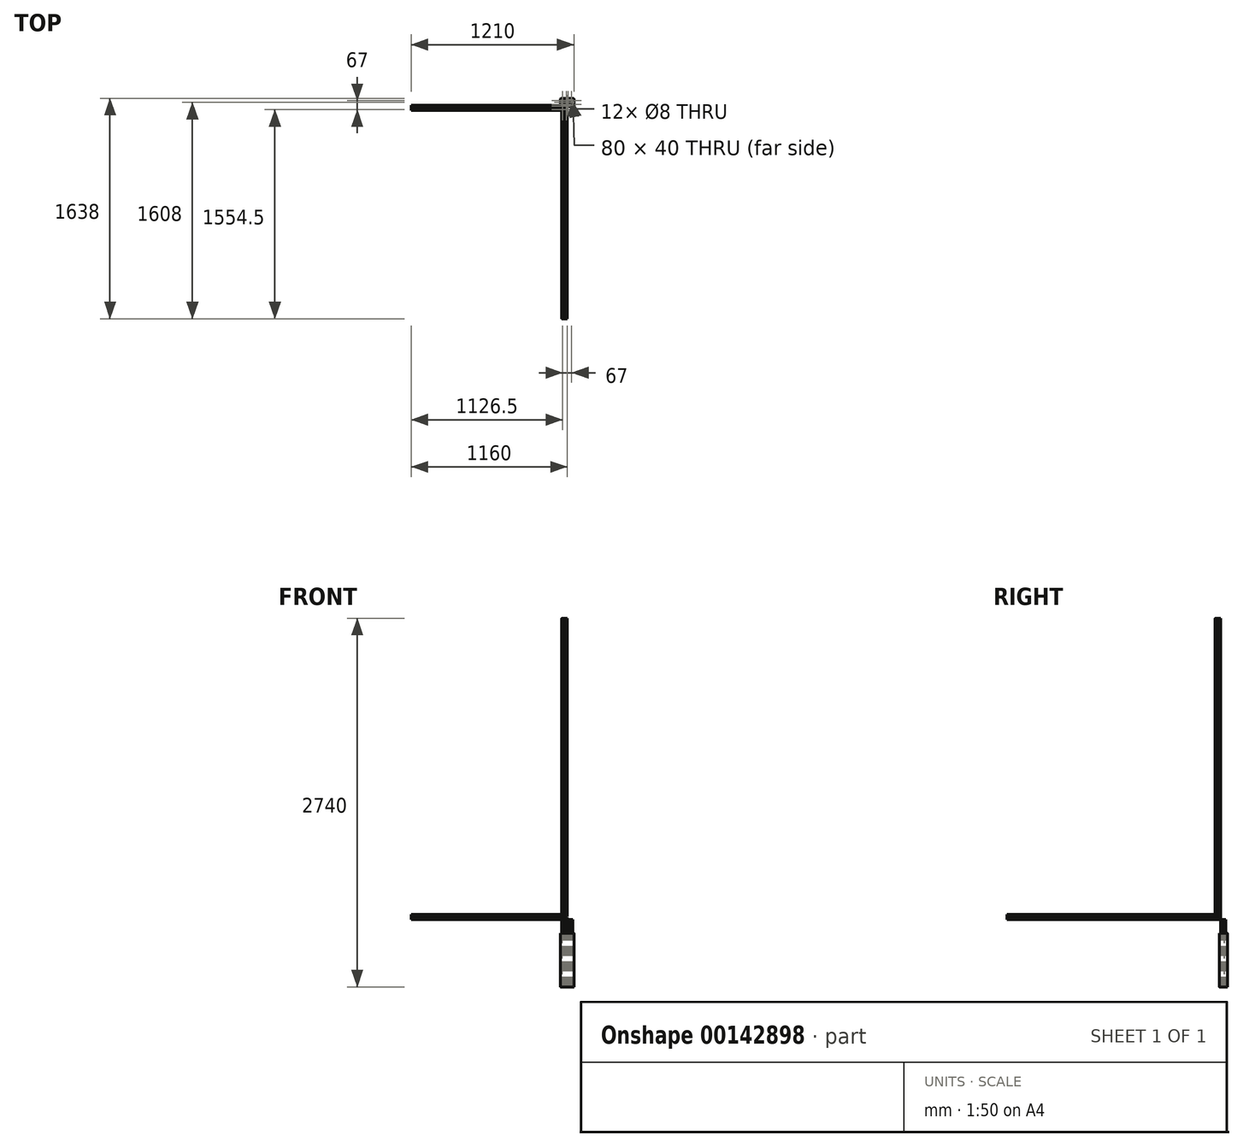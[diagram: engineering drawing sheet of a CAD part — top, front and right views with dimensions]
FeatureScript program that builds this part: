
annotation { "Feature Type Name" : "Feature", "Feature Type Description" : "" }
export const myFeature = defineFeature(function(context is Context, id is Id, definition is map)
    precondition{}
    {
        {
            var Q0;
            Q0=qCreatedBy(makeId("Front.planeOp"),FACE);
            var sketch = newSketch(context, id + "F0", { "sketchPlane" : qUnion([Q0])});
            skArc(sketch, "E0", {"start": v(-0.25, 3.4) * mm, "mid": v(-2.94, 1.7) * mm, "end": v(-3.06, -1.48) * mm});
            skArc(sketch, "E1", {"start": v(0.25, 3.4) * mm, "mid": v(0, 3.65) * mm, "end": v(-0.25, 3.4) * mm});
            skArc(sketch, "E2.1.0", {"start": v(-3.06, -1.48) * mm, "mid": v(-3.16, -1.82) * mm, "end": v(-2.81, -1.91) * mm});
            skArc(sketch, "E2.2.0", {"start": v(2.81, -1.91) * mm, "mid": v(3.16, -1.82) * mm, "end": v(3.06, -1.48) * mm});
            skArc(sketch, "E3.trimOffspring", {"start": v(3.06, -1.48) * mm, "mid": v(2.94, 1.7) * mm, "end": v(0.25, 3.4) * mm});
            skArc(sketch, "E4.trimOffspring", {"start": v(-2.81, -1.91) * mm, "mid": v(0, -3.4) * mm, "end": v(2.81, -1.91) * mm});
            skCircle(sketch, "E5", {"center": v(-13.5, 13.5) * mm, "radius": 4 * mm});
            skCircle(sketch, "E6.1.0", {"center": v(-13.5, -13.5) * mm, "radius": 4 * mm});
            skCircle(sketch, "E6.2.0", {"center": v(13.5, -13.5) * mm, "radius": 4 * mm});
            skCircle(sketch, "E6.3.0", {"center": v(13.5, 13.5) * mm, "radius": 4 * mm});
            skLineSegment(sketch, "E7.rect.bottom", {"start": v(19, -20) * mm, "end": v(-19, -20) * mm});
            skLineSegment(sketch, "E7.rect.top", {"start": v(19, 20) * mm, "end": v(4.2, 20) * mm});
            skLineSegment(sketch, "E7.rect.left", {"start": v(20, -19) * mm, "end": v(20, 19) * mm});
            skLineSegment(sketch, "E7.rect.right", {"start": v(-20, -19) * mm, "end": v(-20, 19) * mm});
            skPoint(sketch, "E8.visualSharp", {"position": v(-20, 20) * mm});
            skArc(sketch, "E8.filletArc", {"start": v(-19, 20) * mm, "mid": v(-19.7, 19.7) * mm, "end": v(-20, 19) * mm});
            skPoint(sketch, "E9.visualSharp", {"position": v(20, 20) * mm});
            skArc(sketch, "E9.filletArc", {"start": v(20, 19) * mm, "mid": v(19.7, 19.7) * mm, "end": v(19, 20) * mm});
            skPoint(sketch, "E10.visualSharp", {"position": v(-20, -20) * mm});
            skArc(sketch, "E10.filletArc", {"start": v(-20, -19) * mm, "mid": v(-19.7, -19.7) * mm, "end": v(-19, -20) * mm});
            skPoint(sketch, "E11.visualSharp", {"position": v(20, -20) * mm});
            skArc(sketch, "E11.filletArc", {"start": v(19, -20) * mm, "mid": v(19.7, -19.7) * mm, "end": v(20, -19) * mm});
            skLineSegment(sketch, "E12.rect.bottom", {"start": v(-16, -4.2) * mm, "end": v(-20, -4.2) * mm});
            skLineSegment(sketch, "E12.rect.top", {"start": v(-16, 4.2) * mm, "end": v(-20, 4.2) * mm});
            skLineSegment(sketch, "E12.rect.right", {"start": v(-20, -4.2) * mm, "end": v(-20, 4.2) * mm});
            skPoint(sketch, "E12.rect.middle", {"position": v(-18, 0) * mm});
            skLineSegment(sketch, "E13.rect.bottom", {"start": v(-16, 7.25) * mm, "end": v(-9.36, 7.25) * mm});
            skLineSegment(sketch, "E13.rect.top", {"start": v(-16, -7.25) * mm, "end": v(-9.36, -7.25) * mm});
            skLineSegment(sketch, "E13.rect.left", {"start": v(-16, 7.25) * mm, "end": v(-16, 4.2) * mm});
            skPoint(sketch, "E13.rect.middle", {"position": v(-12.68, 0) * mm});
            skPoint(sketch, "E13.rect.middle.positionSnap0", {"position": v(-16, 0) * mm});
            skPoint(sketch, "E13.rect.cornerSnap0", {"position": v(-16, 0) * mm});
            skPoint(sketch, "E13.rect.centerSnap0", {"position": v(-16, 0) * mm});
            skLineSegment(sketch, "E14.trimOffspring", {"start": v(-16, -4.2) * mm, "end": v(-16, -7.25) * mm});
            skArc(sketch, "E15", {"start": v(-9.36, 7.25) * mm, "mid": v(-6, 0) * mm, "end": v(-9.36, -7.25) * mm});
            skLineSegment(sketch, "E16.1.0", {"start": v(4.2, -16) * mm, "end": v(7.25, -16) * mm});
            skLineSegment(sketch, "E16.1.1", {"start": v(4.2, -16) * mm, "end": v(4.2, -20) * mm});
            skPoint(sketch, "E16.1.2", {"position": v(0, -16) * mm});
            skLineSegment(sketch, "E16.1.3", {"start": v(-7.25, -16) * mm, "end": v(-4.2, -16) * mm});
            skPoint(sketch, "E16.1.4", {"position": v(0, -18) * mm});
            skLineSegment(sketch, "E16.1.5", {"start": v(7.25, -16) * mm, "end": v(7.25, -9.36) * mm});
            skArc(sketch, "E16.1.6", {"start": v(-7.25, -9.36) * mm, "mid": v(0, -6) * mm, "end": v(7.25, -9.36) * mm});
            skLineSegment(sketch, "E16.1.7", {"start": v(-7.25, -16) * mm, "end": v(-7.25, -9.36) * mm});
            skLineSegment(sketch, "E16.1.8", {"start": v(4.2, -20) * mm, "end": v(-4.2, -20) * mm});
            skLineSegment(sketch, "E16.1.9", {"start": v(-4.2, -16) * mm, "end": v(-4.2, -20) * mm});
            skPoint(sketch, "E16.1.10", {"position": v(0, -12.68) * mm});
            skPoint(sketch, "E16.1.11", {"position": v(0, -16) * mm});
            skPoint(sketch, "E16.1.12", {"position": v(0, -16) * mm});
            skLineSegment(sketch, "E16.2.0", {"start": v(16, 4.2) * mm, "end": v(16, 7.25) * mm});
            skLineSegment(sketch, "E16.2.1", {"start": v(16, 4.2) * mm, "end": v(20, 4.2) * mm});
            skPoint(sketch, "E16.2.2", {"position": v(16, 0) * mm});
            skLineSegment(sketch, "E16.2.3", {"start": v(16, -7.25) * mm, "end": v(16, -4.2) * mm});
            skPoint(sketch, "E16.2.4", {"position": v(18, 0) * mm});
            skLineSegment(sketch, "E16.2.5", {"start": v(16, 7.25) * mm, "end": v(9.36, 7.25) * mm});
            skArc(sketch, "E16.2.6", {"start": v(9.36, -7.25) * mm, "mid": v(6, 0) * mm, "end": v(9.36, 7.25) * mm});
            skLineSegment(sketch, "E16.2.7", {"start": v(16, -7.25) * mm, "end": v(9.36, -7.25) * mm});
            skLineSegment(sketch, "E16.2.8", {"start": v(20, 4.2) * mm, "end": v(20, -4.2) * mm});
            skLineSegment(sketch, "E16.2.9", {"start": v(16, -4.2) * mm, "end": v(20, -4.2) * mm});
            skPoint(sketch, "E16.2.10", {"position": v(12.68, 0) * mm});
            skPoint(sketch, "E16.2.11", {"position": v(16, 0) * mm});
            skPoint(sketch, "E16.2.12", {"position": v(16, 0) * mm});
            skLineSegment(sketch, "E16.3.0", {"start": v(-4.2, 16) * mm, "end": v(-7.25, 16) * mm});
            skLineSegment(sketch, "E16.3.1", {"start": v(-4.2, 16) * mm, "end": v(-4.2, 20) * mm});
            skPoint(sketch, "E16.3.2", {"position": v(0, 16) * mm});
            skLineSegment(sketch, "E16.3.3", {"start": v(7.25, 16) * mm, "end": v(4.2, 16) * mm});
            skPoint(sketch, "E16.3.4", {"position": v(0, 18) * mm});
            skLineSegment(sketch, "E16.3.5", {"start": v(-7.25, 16) * mm, "end": v(-7.25, 9.36) * mm});
            skArc(sketch, "E16.3.6", {"start": v(7.25, 9.36) * mm, "mid": v(0, 6) * mm, "end": v(-7.25, 9.36) * mm});
            skLineSegment(sketch, "E16.3.7", {"start": v(7.25, 16) * mm, "end": v(7.25, 9.36) * mm});
            skLineSegment(sketch, "E16.3.8", {"start": v(-4.2, 20) * mm, "end": v(4.2, 20) * mm});
            skLineSegment(sketch, "E16.3.9", {"start": v(4.2, 16) * mm, "end": v(4.2, 20) * mm});
            skPoint(sketch, "E16.3.10", {"position": v(0, 12.68) * mm});
            skPoint(sketch, "E16.3.11", {"position": v(0, 16) * mm});
            skPoint(sketch, "E16.3.12", {"position": v(0, 16) * mm});
            skLineSegment(sketch, "E17.trimOffspring", {"start": v(-4.2, 20) * mm, "end": v(-19, 20) * mm});
            skSolve(sketch);
        }
        {
            var Q0;
            Q0=makeQuery(id+"F0.imprint","IMPRINT",FACE,{"disambiguationData":[TD([[makeQuery(id+"F0.imprint","IMPRINT",EDGE,{"derivedFrom":sQuery(id+"F0.wireOp",EDGE,"E0")}),-1.0]])]});
            extrude(context, id + "F1", {"entities" : qUnion([Q0]), "depth" : 1588 * mm});
        }
        {
            var Q0;
            Q0=makeQuery(id+"F0.imprint","IMPRINT",FACE,{"disambiguationData":[TD([[makeQuery(id+"F0.imprint","IMPRINT",EDGE,{"derivedFrom":sQuery(id+"F0.wireOp",EDGE,"E0")}),-1.0]])]});
            extrude(context, id + "F2", {"entities" : qUnion([Q0]), "depth" : 2200 * mm});
        }
        {
            var Q0;
            Q0=makeQuery(id+"F2.opExtrude","SWEPT_BODY",BODY,{"disambiguationData":[OSD([sQuery(id+"F0.wireOp",EDGE,"E0"),sQuery(id+"F0.wireOp",EDGE,"E1"),sQuery(id+"F0.wireOp",EDGE,"E2.1.0"),sQuery(id+"F0.wireOp",EDGE,"E2.2.0"),sQuery(id+"F0.wireOp",EDGE,"E3.trimOffspring"),sQuery(id+"F0.wireOp",EDGE,"E4.trimOffspring"),sQuery(id+"F0.wireOp",EDGE,"E5"),sQuery(id+"F0.wireOp",EDGE,"E6.1.0"),sQuery(id+"F0.wireOp",EDGE,"E6.2.0"),sQuery(id+"F0.wireOp",EDGE,"E6.3.0"),sQuery(id+"F0.wireOp",EDGE,"E7.rect.bottom"),sQuery(id+"F0.wireOp",EDGE,"E7.rect.top"),sQuery(id+"F0.wireOp",EDGE,"E7.rect.left"),sQuery(id+"F0.wireOp",EDGE,"E7.rect.right"),sQuery(id+"F0.wireOp",EDGE,"E8.filletArc"),sQuery(id+"F0.wireOp",EDGE,"E9.filletArc"),sQuery(id+"F0.wireOp",EDGE,"E10.filletArc"),sQuery(id+"F0.wireOp",EDGE,"E11.filletArc"),sQuery(id+"F0.wireOp",EDGE,"E12.rect.bottom"),sQuery(id+"F0.wireOp",EDGE,"E12.rect.top"),sQuery(id+"F0.wireOp",EDGE,"E13.rect.bottom"),sQuery(id+"F0.wireOp",EDGE,"E13.rect.top"),sQuery(id+"F0.wireOp",EDGE,"E13.rect.left"),sQuery(id+"F0.wireOp",EDGE,"E14.trimOffspring"),sQuery(id+"F0.wireOp",EDGE,"E15"),sQuery(id+"F0.wireOp",EDGE,"E16.1.0"),sQuery(id+"F0.wireOp",EDGE,"E16.1.1"),sQuery(id+"F0.wireOp",EDGE,"E16.1.3"),sQuery(id+"F0.wireOp",EDGE,"E16.1.5"),sQuery(id+"F0.wireOp",EDGE,"E16.1.6"),sQuery(id+"F0.wireOp",EDGE,"E16.1.7"),sQuery(id+"F0.wireOp",EDGE,"E16.1.9"),sQuery(id+"F0.wireOp",EDGE,"E16.2.0"),sQuery(id+"F0.wireOp",EDGE,"E16.2.1"),sQuery(id+"F0.wireOp",EDGE,"E16.2.3"),sQuery(id+"F0.wireOp",EDGE,"E16.2.5"),sQuery(id+"F0.wireOp",EDGE,"E16.2.6"),sQuery(id+"F0.wireOp",EDGE,"E16.2.7"),sQuery(id+"F0.wireOp",EDGE,"E16.2.9"),sQuery(id+"F0.wireOp",EDGE,"E16.3.0"),sQuery(id+"F0.wireOp",EDGE,"E16.3.1"),sQuery(id+"F0.wireOp",EDGE,"E16.3.3"),sQuery(id+"F0.wireOp",EDGE,"E16.3.5"),sQuery(id+"F0.wireOp",EDGE,"E16.3.6"),sQuery(id+"F0.wireOp",EDGE,"E16.3.7"),sQuery(id+"F0.wireOp",EDGE,"E16.3.9"),sQuery(id+"F0.wireOp",EDGE,"E17.trimOffspring")])]});
            var Q1;
            Q1=sQuery(id+"F0.wireOp",EDGE,"E7.rect.top");
            transform(context, id + "F3", {"entities" : qUnion([Q0]), "transformType" : TransformType.ROTATION, "transformAxis" : qUnion([Q1]), "angle" : 90 * degree, "makeCopy" : false});
        }
        {
            var Q0;
            Q0=makeQuery(id+"F0.imprint","IMPRINT",FACE,{"disambiguationData":[TD([[makeQuery(id+"F0.imprint","IMPRINT",EDGE,{"derivedFrom":sQuery(id+"F0.wireOp",EDGE,"E0")}),-1.0]])]});
            extrude(context, id + "F4", {"entities" : qUnion([Q0]), "depth" : 1120 * mm});
        }
        {
            var Q0;
            Q0=makeQuery(id+"F4.opExtrude","SWEPT_BODY",BODY,{"disambiguationData":[OSD([sQuery(id+"F0.wireOp",EDGE,"E0"),sQuery(id+"F0.wireOp",EDGE,"E1"),sQuery(id+"F0.wireOp",EDGE,"E2.1.0"),sQuery(id+"F0.wireOp",EDGE,"E2.2.0"),sQuery(id+"F0.wireOp",EDGE,"E3.trimOffspring"),sQuery(id+"F0.wireOp",EDGE,"E4.trimOffspring"),sQuery(id+"F0.wireOp",EDGE,"E5"),sQuery(id+"F0.wireOp",EDGE,"E6.1.0"),sQuery(id+"F0.wireOp",EDGE,"E6.2.0"),sQuery(id+"F0.wireOp",EDGE,"E6.3.0"),sQuery(id+"F0.wireOp",EDGE,"E7.rect.bottom"),sQuery(id+"F0.wireOp",EDGE,"E7.rect.top"),sQuery(id+"F0.wireOp",EDGE,"E7.rect.left"),sQuery(id+"F0.wireOp",EDGE,"E7.rect.right"),sQuery(id+"F0.wireOp",EDGE,"E8.filletArc"),sQuery(id+"F0.wireOp",EDGE,"E9.filletArc"),sQuery(id+"F0.wireOp",EDGE,"E10.filletArc"),sQuery(id+"F0.wireOp",EDGE,"E11.filletArc"),sQuery(id+"F0.wireOp",EDGE,"E12.rect.bottom"),sQuery(id+"F0.wireOp",EDGE,"E12.rect.top"),sQuery(id+"F0.wireOp",EDGE,"E13.rect.bottom"),sQuery(id+"F0.wireOp",EDGE,"E13.rect.top"),sQuery(id+"F0.wireOp",EDGE,"E13.rect.left"),sQuery(id+"F0.wireOp",EDGE,"E14.trimOffspring"),sQuery(id+"F0.wireOp",EDGE,"E15"),sQuery(id+"F0.wireOp",EDGE,"E16.1.0"),sQuery(id+"F0.wireOp",EDGE,"E16.1.1"),sQuery(id+"F0.wireOp",EDGE,"E16.1.3"),sQuery(id+"F0.wireOp",EDGE,"E16.1.5"),sQuery(id+"F0.wireOp",EDGE,"E16.1.6"),sQuery(id+"F0.wireOp",EDGE,"E16.1.7"),sQuery(id+"F0.wireOp",EDGE,"E16.1.9"),sQuery(id+"F0.wireOp",EDGE,"E16.2.0"),sQuery(id+"F0.wireOp",EDGE,"E16.2.1"),sQuery(id+"F0.wireOp",EDGE,"E16.2.3"),sQuery(id+"F0.wireOp",EDGE,"E16.2.5"),sQuery(id+"F0.wireOp",EDGE,"E16.2.6"),sQuery(id+"F0.wireOp",EDGE,"E16.2.7"),sQuery(id+"F0.wireOp",EDGE,"E16.2.9"),sQuery(id+"F0.wireOp",EDGE,"E16.3.0"),sQuery(id+"F0.wireOp",EDGE,"E16.3.1"),sQuery(id+"F0.wireOp",EDGE,"E16.3.3"),sQuery(id+"F0.wireOp",EDGE,"E16.3.5"),sQuery(id+"F0.wireOp",EDGE,"E16.3.6"),sQuery(id+"F0.wireOp",EDGE,"E16.3.7"),sQuery(id+"F0.wireOp",EDGE,"E16.3.9"),sQuery(id+"F0.wireOp",EDGE,"E17.trimOffspring")])]});
            var Q1;
            Q1=sQuery(id+"F0.wireOp",EDGE,"E7.rect.right");
            transform(context, id + "F5", {"entities" : qUnion([Q0]), "transformType" : TransformType.ROTATION, "transformAxis" : qUnion([Q1]), "angle" : 90 * degree, "oppositeDirection" : true, "makeCopy" : false});
        }
        {
            var Q0;
            Q0=makeQuery(id+"F0.imprint","IMPRINT",FACE,{"disambiguationData":[TD([[makeQuery(id+"F0.imprint","IMPRINT",EDGE,{"derivedFrom":sQuery(id+"F0.wireOp",EDGE,"E0")}),-1.0]])]});
            extrude(context, id + "F6", {"entities" : qUnion([Q0]), "oppositeDirection" : true, "depth" : 500 * mm});
        }
        {
            var Q0;
            Q0=makeQuery(id+"F6.opExtrude","SWEPT_BODY",BODY,{"disambiguationData":[OSD([sQuery(id+"F0.wireOp",EDGE,"E0"),sQuery(id+"F0.wireOp",EDGE,"E1"),sQuery(id+"F0.wireOp",EDGE,"E2.1.0"),sQuery(id+"F0.wireOp",EDGE,"E2.2.0"),sQuery(id+"F0.wireOp",EDGE,"E3.trimOffspring"),sQuery(id+"F0.wireOp",EDGE,"E4.trimOffspring"),sQuery(id+"F0.wireOp",EDGE,"E5"),sQuery(id+"F0.wireOp",EDGE,"E6.1.0"),sQuery(id+"F0.wireOp",EDGE,"E6.2.0"),sQuery(id+"F0.wireOp",EDGE,"E6.3.0"),sQuery(id+"F0.wireOp",EDGE,"E7.rect.bottom"),sQuery(id+"F0.wireOp",EDGE,"E7.rect.top"),sQuery(id+"F0.wireOp",EDGE,"E7.rect.left"),sQuery(id+"F0.wireOp",EDGE,"E7.rect.right"),sQuery(id+"F0.wireOp",EDGE,"E8.filletArc"),sQuery(id+"F0.wireOp",EDGE,"E9.filletArc"),sQuery(id+"F0.wireOp",EDGE,"E10.filletArc"),sQuery(id+"F0.wireOp",EDGE,"E11.filletArc"),sQuery(id+"F0.wireOp",EDGE,"E12.rect.bottom"),sQuery(id+"F0.wireOp",EDGE,"E12.rect.top"),sQuery(id+"F0.wireOp",EDGE,"E13.rect.bottom"),sQuery(id+"F0.wireOp",EDGE,"E13.rect.top"),sQuery(id+"F0.wireOp",EDGE,"E13.rect.left"),sQuery(id+"F0.wireOp",EDGE,"E14.trimOffspring"),sQuery(id+"F0.wireOp",EDGE,"E15"),sQuery(id+"F0.wireOp",EDGE,"E16.1.0"),sQuery(id+"F0.wireOp",EDGE,"E16.1.1"),sQuery(id+"F0.wireOp",EDGE,"E16.1.3"),sQuery(id+"F0.wireOp",EDGE,"E16.1.5"),sQuery(id+"F0.wireOp",EDGE,"E16.1.6"),sQuery(id+"F0.wireOp",EDGE,"E16.1.7"),sQuery(id+"F0.wireOp",EDGE,"E16.1.9"),sQuery(id+"F0.wireOp",EDGE,"E16.2.0"),sQuery(id+"F0.wireOp",EDGE,"E16.2.1"),sQuery(id+"F0.wireOp",EDGE,"E16.2.3"),sQuery(id+"F0.wireOp",EDGE,"E16.2.5"),sQuery(id+"F0.wireOp",EDGE,"E16.2.6"),sQuery(id+"F0.wireOp",EDGE,"E16.2.7"),sQuery(id+"F0.wireOp",EDGE,"E16.2.9"),sQuery(id+"F0.wireOp",EDGE,"E16.3.0"),sQuery(id+"F0.wireOp",EDGE,"E16.3.1"),sQuery(id+"F0.wireOp",EDGE,"E16.3.3"),sQuery(id+"F0.wireOp",EDGE,"E16.3.5"),sQuery(id+"F0.wireOp",EDGE,"E16.3.6"),sQuery(id+"F0.wireOp",EDGE,"E16.3.7"),sQuery(id+"F0.wireOp",EDGE,"E16.3.9"),sQuery(id+"F0.wireOp",EDGE,"E17.trimOffspring")])]});
            var Q1;
            Q1=sQuery(id+"F0.wireOp",EDGE,"E7.rect.bottom");
            var Q2;
            Q2=sQuery(id+"F0.wireOp",EDGE,"E16.1.8");
            transform(context, id + "F7", {"entities" : qUnion([Q0]), "transformType" : TransformType.ROTATION, "transformAxis" : qUnion([Q2]), "angle" : 90 * degree, "makeCopy" : false});
        }
        {
            var Q0;
            Q0=makeQuery(id+"F0.imprint","IMPRINT",FACE,{"disambiguationData":[TD([[makeQuery(id+"F0.imprint","IMPRINT",EDGE,{"derivedFrom":sQuery(id+"F0.wireOp",EDGE,"E0")}),-1.0]])]});
            extrude(context, id + "F8", {"entities" : qUnion([Q0]), "depth" : 30 * mm});
        }
        {
            var Q0;
            Q0=makeQuery(id+"F6.opExtrude","CAP_FACE",FACE,{"disambiguationData":[OSD([sQuery(id+"F0.wireOp",EDGE,"E0"),sQuery(id+"F0.wireOp",EDGE,"E1"),sQuery(id+"F0.wireOp",EDGE,"E2.1.0"),sQuery(id+"F0.wireOp",EDGE,"E2.2.0"),sQuery(id+"F0.wireOp",EDGE,"E3.trimOffspring"),sQuery(id+"F0.wireOp",EDGE,"E4.trimOffspring"),sQuery(id+"F0.wireOp",EDGE,"E5"),sQuery(id+"F0.wireOp",EDGE,"E6.1.0"),sQuery(id+"F0.wireOp",EDGE,"E6.2.0"),sQuery(id+"F0.wireOp",EDGE,"E6.3.0"),sQuery(id+"F0.wireOp",EDGE,"E7.rect.bottom"),sQuery(id+"F0.wireOp",EDGE,"E7.rect.top"),sQuery(id+"F0.wireOp",EDGE,"E7.rect.left"),sQuery(id+"F0.wireOp",EDGE,"E7.rect.right"),sQuery(id+"F0.wireOp",EDGE,"E8.filletArc"),sQuery(id+"F0.wireOp",EDGE,"E9.filletArc"),sQuery(id+"F0.wireOp",EDGE,"E10.filletArc"),sQuery(id+"F0.wireOp",EDGE,"E11.filletArc"),sQuery(id+"F0.wireOp",EDGE,"E12.rect.bottom"),sQuery(id+"F0.wireOp",EDGE,"E12.rect.top"),sQuery(id+"F0.wireOp",EDGE,"E13.rect.bottom"),sQuery(id+"F0.wireOp",EDGE,"E13.rect.top"),sQuery(id+"F0.wireOp",EDGE,"E13.rect.left"),sQuery(id+"F0.wireOp",EDGE,"E14.trimOffspring"),sQuery(id+"F0.wireOp",EDGE,"E15"),sQuery(id+"F0.wireOp",EDGE,"E16.1.0"),sQuery(id+"F0.wireOp",EDGE,"E16.1.1"),sQuery(id+"F0.wireOp",EDGE,"E16.1.3"),sQuery(id+"F0.wireOp",EDGE,"E16.1.5"),sQuery(id+"F0.wireOp",EDGE,"E16.1.6"),sQuery(id+"F0.wireOp",EDGE,"E16.1.7"),sQuery(id+"F0.wireOp",EDGE,"E16.1.9"),sQuery(id+"F0.wireOp",EDGE,"E16.2.0"),sQuery(id+"F0.wireOp",EDGE,"E16.2.1"),sQuery(id+"F0.wireOp",EDGE,"E16.2.3"),sQuery(id+"F0.wireOp",EDGE,"E16.2.5"),sQuery(id+"F0.wireOp",EDGE,"E16.2.6"),sQuery(id+"F0.wireOp",EDGE,"E16.2.7"),sQuery(id+"F0.wireOp",EDGE,"E16.2.9"),sQuery(id+"F0.wireOp",EDGE,"E16.3.0"),sQuery(id+"F0.wireOp",EDGE,"E16.3.1"),sQuery(id+"F0.wireOp",EDGE,"E16.3.3"),sQuery(id+"F0.wireOp",EDGE,"E16.3.5"),sQuery(id+"F0.wireOp",EDGE,"E16.3.6"),sQuery(id+"F0.wireOp",EDGE,"E16.3.7"),sQuery(id+"F0.wireOp",EDGE,"E16.3.9"),sQuery(id+"F0.wireOp",EDGE,"E17.trimOffspring")])],"isStart":false});
            var sketch = newSketch(context, id + "F9", { "sketchPlane" : qUnion([Q0])});
            skLineSegment(sketch, "E18.bottom", {"start": v(20, -40) * mm, "end": v(-20, -40) * mm});
            skLineSegment(sketch, "E18.top", {"start": v(20, 0) * mm, "end": v(-20, 0) * mm});
            skLineSegment(sketch, "E18.left", {"start": v(20, -40) * mm, "end": v(20, 0) * mm});
            skLineSegment(sketch, "E18.right", {"start": v(-20, -40) * mm, "end": v(-20, 0) * mm});
            skPoint(sketch, "E18.middle", {"position": v(0, -20) * mm});
            skLineSegment(sketch, "E19.bottom", {"start": v(30, -50) * mm, "end": v(-30, -50) * mm});
            skLineSegment(sketch, "E19.top", {"start": v(30, 10) * mm, "end": v(-30, 10) * mm});
            skLineSegment(sketch, "E19.left", {"start": v(30, -50) * mm, "end": v(30, 10) * mm});
            skLineSegment(sketch, "E19.right", {"start": v(-30, -50) * mm, "end": v(-30, 10) * mm});
            skSolve(sketch);
        }
        {
            var Q0;
            Q0=makeQuery(id+"F9.imprint","IMPRINT",FACE,{"disambiguationData":[TD([[makeQuery(id+"F9.imprint","IMPRINT",EDGE,{"derivedFrom":sQuery(id+"F9.wireOp",EDGE,"E19.bottom")}),-1.0]])]});
            extrude(context, id + "F10", {"entities" : qUnion([Q0]), "oppositeDirection" : true, "depth" : 400 * mm});
        }
        {
            var Q0;
            Q0=makeQuery(id+"F10.opExtrude","SWEPT_FACE",FACE,{"disambiguationData":[OSD([sQuery(id+"F9.wireOp",EDGE,"E19.right")])]});
            var sketch = newSketch(context, id + "F11", { "sketchPlane" : qUnion([Q0])});
            skLineSegment(sketch, "E20.bottom", {"start": v(-15, -520) * mm, "end": v(-25, -520) * mm});
            skLineSegment(sketch, "E20.top", {"start": v(-15, -120) * mm, "end": v(-25, -120) * mm});
            skLineSegment(sketch, "E20.left", {"start": v(-15, -520) * mm, "end": v(-15, -120) * mm});
            skLineSegment(sketch, "E20.right", {"start": v(-25, -520) * mm, "end": v(-25, -120) * mm});
            skPoint(sketch, "E20.middle", {"position": v(-20, -320) * mm});
            skPoint(sketch, "E20.middle.positionSnap0", {"position": v(10, -320) * mm});
            skPoint(sketch, "E20.middle.positionSnap1", {"position": v(-20, -120) * mm});
            skPoint(sketch, "E20.centerSnap0", {"position": v(10, -320) * mm});
            skPoint(sketch, "E20.centerSnap1", {"position": v(-20, -120) * mm});
            skSolve(sketch);
        }
        {
            var Q0;
            Q0=makeQuery(id+"F11.imprint","IMPRINT",FACE,{"disambiguationData":[TD([[makeQuery(id+"F11.imprint","IMPRINT",EDGE,{"derivedFrom":sQuery(id+"F11.wireOp",EDGE,"E20.bottom")}),1.0]])]});
            extrude(context, id + "F12", {"entities" : qUnion([Q0]), "operationType" : NewBodyOperationType.REMOVE, "oppositeDirection" : true, "depth" : 25 * mm});
        }
        {
            var Q0;
            Q0=makeQuery(id+"F10.opExtrude","SWEPT_EDGE",EDGE,{"disambiguationData":[OSD([sQuery(id+"F9.wireOp",EDGE,"E19.bottom"),sQuery(id+"F9.wireOp",EDGE,"E19.right")])]});
            var Q1;
            Q1=makeQuery(id+"F10.opExtrude","SWEPT_EDGE",EDGE,{"disambiguationData":[OSD([sQuery(id+"F9.wireOp",EDGE,"E19.bottom"),sQuery(id+"F9.wireOp",EDGE,"E19.left")])]});
            var Q2;
            Q2=makeQuery(id+"F10.opExtrude","SWEPT_EDGE",EDGE,{"disambiguationData":[OSD([sQuery(id+"F9.wireOp",EDGE,"E19.top"),sQuery(id+"F9.wireOp",EDGE,"E19.left")])]});
            var Q3;
            Q3=makeQuery(id+"F10.opExtrude","SWEPT_EDGE",EDGE,{"disambiguationData":[OSD([sQuery(id+"F9.wireOp",EDGE,"E19.top"),sQuery(id+"F9.wireOp",EDGE,"E19.right")])]});
            fillet(context, id + "F13", {"entities" : qUnion([Q0, Q1, Q2, Q3]), "radius" : 5 * mm, "tangentPropagation" : true, "allowEdgeOverflow" : false});
        }
        {
            var Q0;
            Q0=makeQuery(id+"F10.opExtrude","SWEPT_BODY",BODY,{"disambiguationData":[OSD([sQuery(id+"F9.wireOp",EDGE,"E18.bottom"),sQuery(id+"F9.wireOp",EDGE,"E18.top"),sQuery(id+"F9.wireOp",EDGE,"E18.left"),sQuery(id+"F9.wireOp",EDGE,"E18.right"),sQuery(id+"F9.wireOp",EDGE,"E19.bottom"),sQuery(id+"F9.wireOp",EDGE,"E19.top"),sQuery(id+"F9.wireOp",EDGE,"E19.left"),sQuery(id+"F9.wireOp",EDGE,"E19.right")])]});
            deleteBodies(context, id + "F14", {"entities" : qUnion([Q0])});
        }
        {
            var Q0;
            Q0=makeQuery(id+"F6.opExtrude","SWEPT_BODY",BODY,{"disambiguationData":[OSD([sQuery(id+"F0.wireOp",EDGE,"E0"),sQuery(id+"F0.wireOp",EDGE,"E1"),sQuery(id+"F0.wireOp",EDGE,"E2.1.0"),sQuery(id+"F0.wireOp",EDGE,"E2.2.0"),sQuery(id+"F0.wireOp",EDGE,"E3.trimOffspring"),sQuery(id+"F0.wireOp",EDGE,"E4.trimOffspring"),sQuery(id+"F0.wireOp",EDGE,"E5"),sQuery(id+"F0.wireOp",EDGE,"E6.1.0"),sQuery(id+"F0.wireOp",EDGE,"E6.2.0"),sQuery(id+"F0.wireOp",EDGE,"E6.3.0"),sQuery(id+"F0.wireOp",EDGE,"E7.rect.bottom"),sQuery(id+"F0.wireOp",EDGE,"E7.rect.top"),sQuery(id+"F0.wireOp",EDGE,"E7.rect.left"),sQuery(id+"F0.wireOp",EDGE,"E7.rect.right"),sQuery(id+"F0.wireOp",EDGE,"E8.filletArc"),sQuery(id+"F0.wireOp",EDGE,"E9.filletArc"),sQuery(id+"F0.wireOp",EDGE,"E10.filletArc"),sQuery(id+"F0.wireOp",EDGE,"E11.filletArc"),sQuery(id+"F0.wireOp",EDGE,"E12.rect.bottom"),sQuery(id+"F0.wireOp",EDGE,"E12.rect.top"),sQuery(id+"F0.wireOp",EDGE,"E13.rect.bottom"),sQuery(id+"F0.wireOp",EDGE,"E13.rect.top"),sQuery(id+"F0.wireOp",EDGE,"E13.rect.left"),sQuery(id+"F0.wireOp",EDGE,"E14.trimOffspring"),sQuery(id+"F0.wireOp",EDGE,"E15"),sQuery(id+"F0.wireOp",EDGE,"E16.1.0"),sQuery(id+"F0.wireOp",EDGE,"E16.1.1"),sQuery(id+"F0.wireOp",EDGE,"E16.1.3"),sQuery(id+"F0.wireOp",EDGE,"E16.1.5"),sQuery(id+"F0.wireOp",EDGE,"E16.1.6"),sQuery(id+"F0.wireOp",EDGE,"E16.1.7"),sQuery(id+"F0.wireOp",EDGE,"E16.1.9"),sQuery(id+"F0.wireOp",EDGE,"E16.2.0"),sQuery(id+"F0.wireOp",EDGE,"E16.2.1"),sQuery(id+"F0.wireOp",EDGE,"E16.2.3"),sQuery(id+"F0.wireOp",EDGE,"E16.2.5"),sQuery(id+"F0.wireOp",EDGE,"E16.2.6"),sQuery(id+"F0.wireOp",EDGE,"E16.2.7"),sQuery(id+"F0.wireOp",EDGE,"E16.2.9"),sQuery(id+"F0.wireOp",EDGE,"E16.3.0"),sQuery(id+"F0.wireOp",EDGE,"E16.3.1"),sQuery(id+"F0.wireOp",EDGE,"E16.3.3"),sQuery(id+"F0.wireOp",EDGE,"E16.3.5"),sQuery(id+"F0.wireOp",EDGE,"E16.3.6"),sQuery(id+"F0.wireOp",EDGE,"E16.3.7"),sQuery(id+"F0.wireOp",EDGE,"E16.3.9"),sQuery(id+"F0.wireOp",EDGE,"E17.trimOffspring")])]});
            transform(context, id + "F15", {"entities" : qUnion([Q0]), "transformType" : TransformType.TRANSLATION_3D, "dx" : 40 * mm, "dy" : 0 * mm, "dz" : 0 * mm, "makeCopy" : true});
        }
        {
            var Q0;
            Q0=makeQuery(id+"F6.opExtrude","CAP_FACE",FACE,{"disambiguationData":[OSD([sQuery(id+"F0.wireOp",EDGE,"E0"),sQuery(id+"F0.wireOp",EDGE,"E1"),sQuery(id+"F0.wireOp",EDGE,"E2.1.0"),sQuery(id+"F0.wireOp",EDGE,"E2.2.0"),sQuery(id+"F0.wireOp",EDGE,"E3.trimOffspring"),sQuery(id+"F0.wireOp",EDGE,"E4.trimOffspring"),sQuery(id+"F0.wireOp",EDGE,"E5"),sQuery(id+"F0.wireOp",EDGE,"E6.1.0"),sQuery(id+"F0.wireOp",EDGE,"E6.2.0"),sQuery(id+"F0.wireOp",EDGE,"E6.3.0"),sQuery(id+"F0.wireOp",EDGE,"E7.rect.bottom"),sQuery(id+"F0.wireOp",EDGE,"E7.rect.top"),sQuery(id+"F0.wireOp",EDGE,"E7.rect.left"),sQuery(id+"F0.wireOp",EDGE,"E7.rect.right"),sQuery(id+"F0.wireOp",EDGE,"E8.filletArc"),sQuery(id+"F0.wireOp",EDGE,"E9.filletArc"),sQuery(id+"F0.wireOp",EDGE,"E10.filletArc"),sQuery(id+"F0.wireOp",EDGE,"E11.filletArc"),sQuery(id+"F0.wireOp",EDGE,"E12.rect.bottom"),sQuery(id+"F0.wireOp",EDGE,"E12.rect.top"),sQuery(id+"F0.wireOp",EDGE,"E13.rect.bottom"),sQuery(id+"F0.wireOp",EDGE,"E13.rect.top"),sQuery(id+"F0.wireOp",EDGE,"E13.rect.left"),sQuery(id+"F0.wireOp",EDGE,"E14.trimOffspring"),sQuery(id+"F0.wireOp",EDGE,"E15"),sQuery(id+"F0.wireOp",EDGE,"E16.1.0"),sQuery(id+"F0.wireOp",EDGE,"E16.1.1"),sQuery(id+"F0.wireOp",EDGE,"E16.1.3"),sQuery(id+"F0.wireOp",EDGE,"E16.1.5"),sQuery(id+"F0.wireOp",EDGE,"E16.1.6"),sQuery(id+"F0.wireOp",EDGE,"E16.1.7"),sQuery(id+"F0.wireOp",EDGE,"E16.1.9"),sQuery(id+"F0.wireOp",EDGE,"E16.2.0"),sQuery(id+"F0.wireOp",EDGE,"E16.2.1"),sQuery(id+"F0.wireOp",EDGE,"E16.2.3"),sQuery(id+"F0.wireOp",EDGE,"E16.2.5"),sQuery(id+"F0.wireOp",EDGE,"E16.2.6"),sQuery(id+"F0.wireOp",EDGE,"E16.2.7"),sQuery(id+"F0.wireOp",EDGE,"E16.2.9"),sQuery(id+"F0.wireOp",EDGE,"E16.3.0"),sQuery(id+"F0.wireOp",EDGE,"E16.3.1"),sQuery(id+"F0.wireOp",EDGE,"E16.3.3"),sQuery(id+"F0.wireOp",EDGE,"E16.3.5"),sQuery(id+"F0.wireOp",EDGE,"E16.3.6"),sQuery(id+"F0.wireOp",EDGE,"E16.3.7"),sQuery(id+"F0.wireOp",EDGE,"E16.3.9"),sQuery(id+"F0.wireOp",EDGE,"E17.trimOffspring")])],"isStart":false});
            var sketch = newSketch(context, id + "F16", { "sketchPlane" : qUnion([Q0])});
            skLineSegment(sketch, "E21.bottom", {"start": v(-20, -40) * mm, "end": v(60, -40) * mm});
            skLineSegment(sketch, "E21.top", {"start": v(-20, 0) * mm, "end": v(60, 0) * mm});
            skLineSegment(sketch, "E21.left", {"start": v(-20, -40) * mm, "end": v(-20, 0) * mm});
            skLineSegment(sketch, "E21.right", {"start": v(60, -40) * mm, "end": v(60, 0) * mm});
            skLineSegment(sketch, "E22.bottom", {"start": v(-30, 10) * mm, "end": v(70, 10) * mm});
            skLineSegment(sketch, "E22.top", {"start": v(-30, -50) * mm, "end": v(70, -50) * mm});
            skLineSegment(sketch, "E22.left", {"start": v(-30, 10) * mm, "end": v(-30, -50) * mm});
            skLineSegment(sketch, "E22.right", {"start": v(70, 10) * mm, "end": v(70, -50) * mm});
            skSolve(sketch);
        }
        {
            var Q0;
            {var subQ6=sQuery(id+"F16.wireOp",EDGE,"E21.right");Q0=makeQuery(id+"F16.imprint","IMPRINT",FACE,{"disambiguationData":[TD([[makeQuery(id+"F16.imprint","IMPRINT",EDGE,{"derivedFrom":subQ6}),-1.0]])]});}
            extrude(context, id + "F17", {"entities" : qUnion([Q0]), "oppositeDirection" : true, "depth" : 400 * mm});
        }
        {
            var Q0;
            Q0=makeQuery(id+"F17.opExtrude","SWEPT_EDGE",EDGE,{"disambiguationData":[OSD([sQuery(id+"F16.wireOp",EDGE,"E22.bottom"),sQuery(id+"F16.wireOp",EDGE,"E22.left")])]});
            var Q1;
            Q1=makeQuery(id+"F17.opExtrude","SWEPT_EDGE",EDGE,{"disambiguationData":[OSD([sQuery(id+"F16.wireOp",EDGE,"E22.top"),sQuery(id+"F16.wireOp",EDGE,"E22.left")])]});
            var Q2;
            Q2=makeQuery(id+"F17.opExtrude","SWEPT_EDGE",EDGE,{"disambiguationData":[OSD([sQuery(id+"F16.wireOp",EDGE,"E22.top"),sQuery(id+"F16.wireOp",EDGE,"E22.right")])]});
            var Q3;
            Q3=makeQuery(id+"F17.opExtrude","SWEPT_EDGE",EDGE,{"disambiguationData":[OSD([sQuery(id+"F16.wireOp",EDGE,"E22.bottom"),sQuery(id+"F16.wireOp",EDGE,"E22.right")])]});
            fillet(context, id + "F18", {"entities" : qUnion([Q0, Q1, Q2, Q3]), "radius" : 5 * mm, "tangentPropagation" : true, "allowEdgeOverflow" : false});
        }
    });
